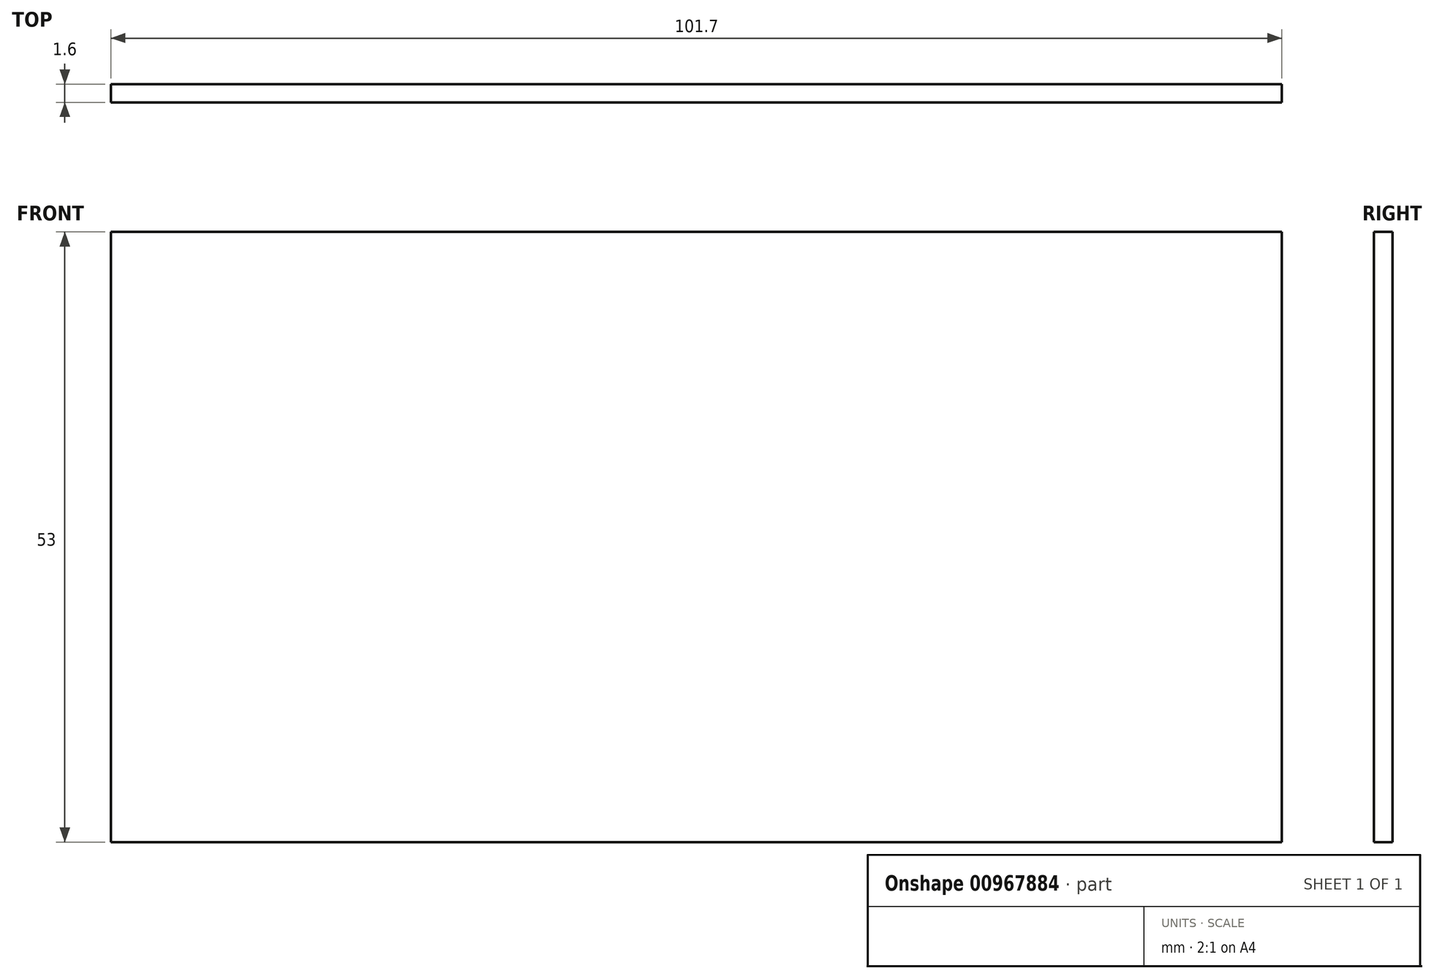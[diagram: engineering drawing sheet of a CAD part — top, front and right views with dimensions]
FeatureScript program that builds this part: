
annotation { "Feature Type Name" : "Feature", "Feature Type Description" : "" }
export const myFeature = defineFeature(function(context is Context, id is Id, definition is map)
    precondition{}
    {
        {
            var Q0;
            Q0=qCreatedBy(makeId("Front.planeOp"),FACE);
            var sketch = newSketch(context, id + "F0", { "sketchPlane" : qUnion([Q0])});
            skLineSegment(sketch, "E0.bottom", {"start": v(50.85, -25) * mm, "end": v(-50.85, -25) * mm});
            skLineSegment(sketch, "E0.top", {"start": v(50.85, 25) * mm, "end": v(-50.85, 25) * mm});
            skLineSegment(sketch, "E0.left", {"start": v(50.85, -25) * mm, "end": v(50.85, 25) * mm});
            skLineSegment(sketch, "E0.right", {"start": v(-50.85, -25) * mm, "end": v(-50.85, 25) * mm});
            skPoint(sketch, "E0.middle", {"position": v(0, 0) * mm});
            skSolve(sketch);
        }
        {
            var Q0;
            Q0=makeQuery(id+"F0.imprint","IMPRINT",FACE,{"disambiguationData":[TD([[makeQuery(id+"F0.imprint","IMPRINT",EDGE,{"derivedFrom":sQuery(id+"F0.wireOp",EDGE,"E0.bottom")}),-1.0]])]});
            extrude(context, id + "F1", {"entities" : qUnion([Q0]), "depth" : 1.6 * mm, "offsetDistance" : 25 * mm});
        }
        {
            var Q0;
            Q0=makeQuery(id+"F1.opExtrude","SWEPT_FACE",FACE,{"disambiguationData":[OSD([sQuery(id+"F0.wireOp",EDGE,"E0.top")])]});
            extrude(context, id + "F2", {"entities" : qUnion([Q0]), "operationType" : NewBodyOperationType.ADD, "depth" : 3 * mm, "offsetDistance" : 25 * mm});
        }
    });
